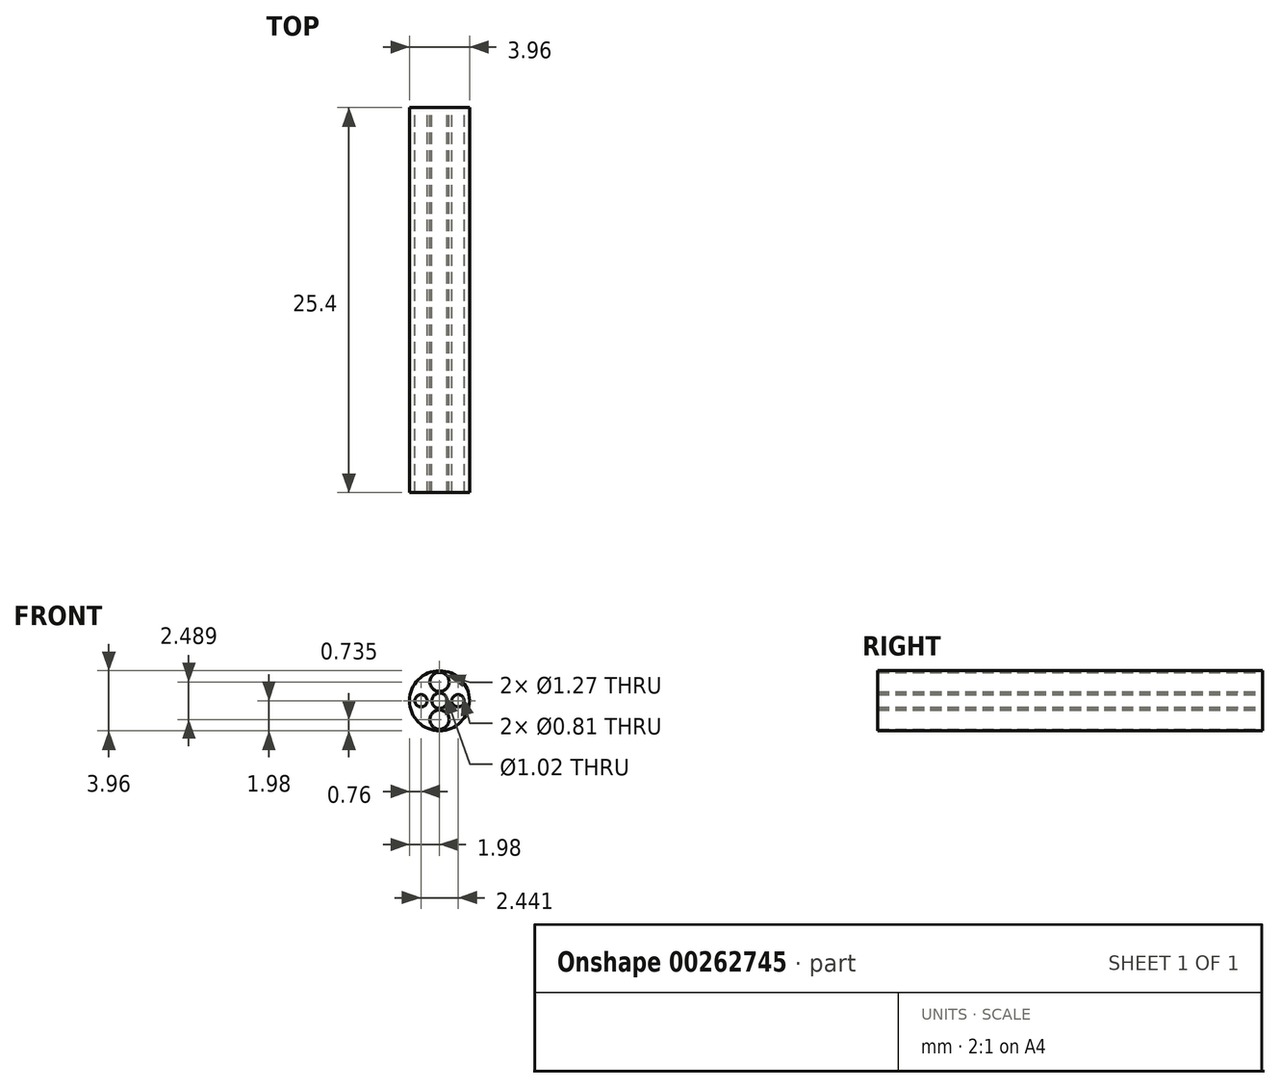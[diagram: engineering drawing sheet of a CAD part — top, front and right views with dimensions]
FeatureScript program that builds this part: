
annotation { "Feature Type Name" : "Feature", "Feature Type Description" : "" }
export const myFeature = defineFeature(function(context is Context, id is Id, definition is map)
    precondition{}
    {
        {
            var Q0;
            Q0=qCreatedBy(makeId("Front.planeOp"),FACE);
            var sketch = newSketch(context, id + "F0", { "sketchPlane" : qUnion([Q0])});
            skCircle(sketch, "E0", {"center": v(0, 0) * mm, "radius": 1.98 * mm});
            skCircle(sketch, "E1", {"center": v(0, 0) * mm, "radius": 0.5 * mm});
            skCircle(sketch, "E2", {"center": v(0, -1.24) * mm, "radius": 0.64 * mm});
            skCircle(sketch, "E3", {"center": v(1.22, 0) * mm, "radius": 0.4 * mm});
            skCircle(sketch, "E4", {"center": v(-1.22, 0) * mm, "radius": 0.4 * mm});
            skLineSegment(sketch, "E5", {"start": v(0, 1.98) * mm, "end": v(0, -1.98) * mm, "construction": true});
            skCircle(sketch, "E6", {"center": v(0, 1.24) * mm, "radius": 0.64 * mm});
            skSolve(sketch);
        }
        {
            var Q0;
            Q0=qSketchRegion(id+"F0",true);
            extrude(context, id + "F1", {"entities" : qUnion([Q0]), "depth" : 25.4 * mm});
        }
    });
